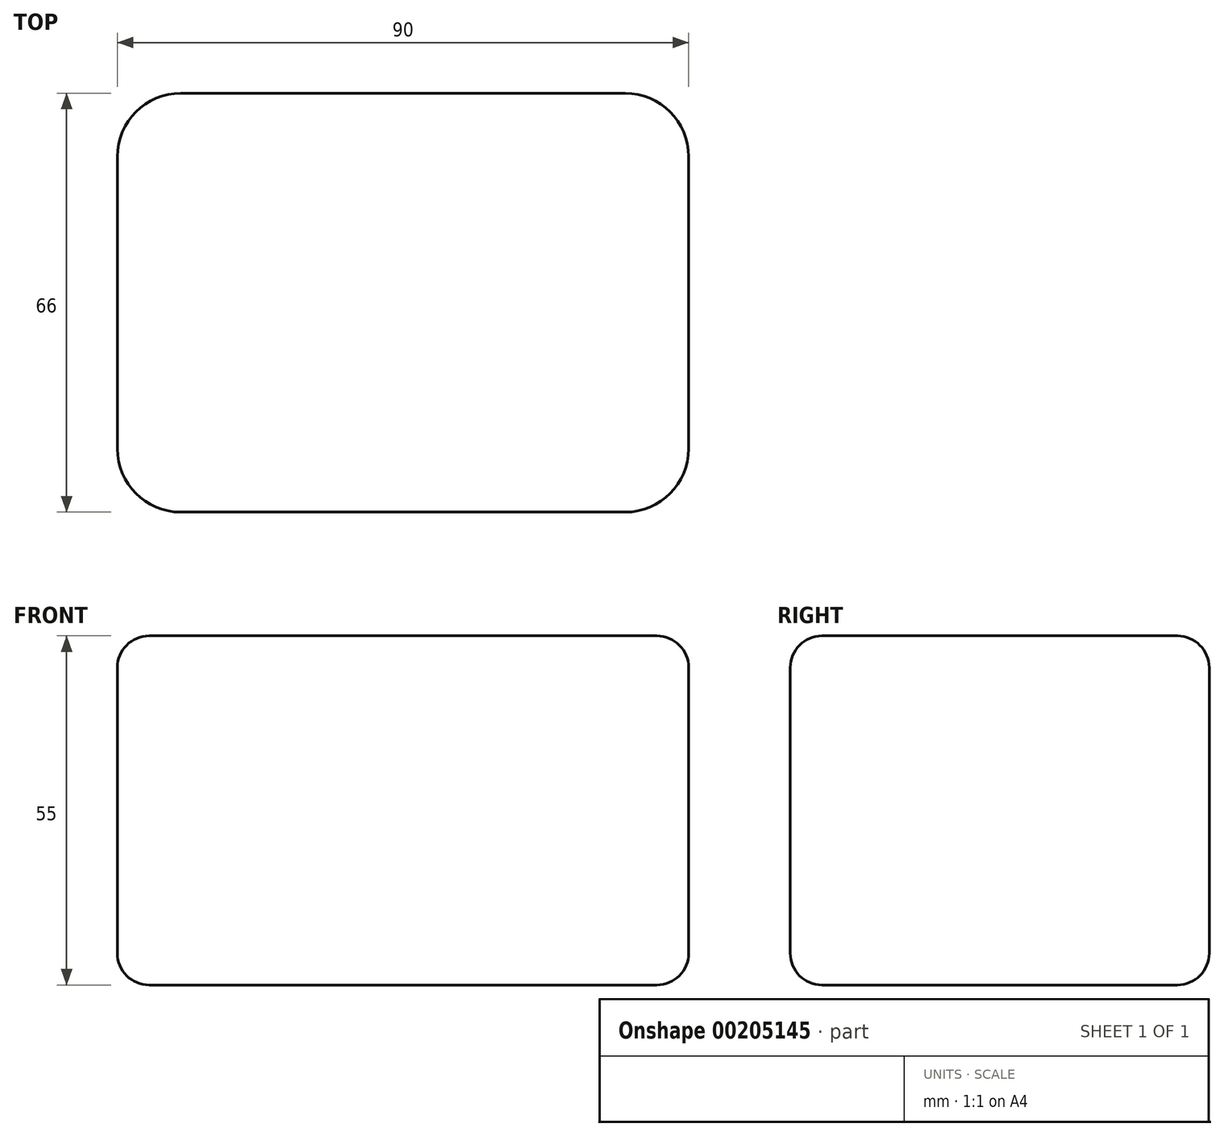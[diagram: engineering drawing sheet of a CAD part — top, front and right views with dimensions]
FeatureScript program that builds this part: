
annotation { "Feature Type Name" : "Feature", "Feature Type Description" : "" }
export const myFeature = defineFeature(function(context is Context, id is Id, definition is map)
    precondition{}
    {
        {
            var Q0;
            Q0=qCreatedBy(makeId("Top.planeOp"),FACE);
            var sketch = newSketch(context, id + "F0", { "sketchPlane" : qUnion([Q0])});
            skLineSegment(sketch, "E0.bottom", {"start": v(0, 0) * mm, "end": v(90, 0) * mm});
            skLineSegment(sketch, "E0.top", {"start": v(0, 66) * mm, "end": v(90, 66) * mm});
            skLineSegment(sketch, "E0.left", {"start": v(0, 0) * mm, "end": v(0, 66) * mm});
            skLineSegment(sketch, "E0.right", {"start": v(90, 0) * mm, "end": v(90, 66) * mm});
            skSolve(sketch);
        }
        {
            var Q0;
            Q0=makeQuery(id+"F0.imprint","IMPRINT",FACE,{"disambiguationData":[TD([[makeQuery(id+"F0.imprint","IMPRINT",EDGE,{"derivedFrom":sQuery(id+"F0.wireOp",EDGE,"E0.bottom")}),1.0]])]});
            extrude(context, id + "F1", {"entities" : qUnion([Q0]), "depth" : 55 * mm});
        }
        {
            var Q0;
            Q0=makeQuery(id+"F1.opExtrude","SWEPT_EDGE",EDGE,{"disambiguationData":[OSD([sQuery(id+"F0.wireOp",EDGE,"E0.bottom"),sQuery(id+"F0.wireOp",EDGE,"E0.right")])]});
            var Q1;
            Q1=makeQuery(id+"F1.opExtrude","SWEPT_EDGE",EDGE,{"disambiguationData":[OSD([sQuery(id+"F0.wireOp",EDGE,"E0.top"),sQuery(id+"F0.wireOp",EDGE,"E0.right")])]});
            var Q2;
            Q2=makeQuery(id+"F1.opExtrude","SWEPT_EDGE",EDGE,{"disambiguationData":[OSD([sQuery(id+"F0.wireOp",EDGE,"E0.top"),sQuery(id+"F0.wireOp",EDGE,"E0.left")])]});
            var Q3;
            Q3=makeQuery(id+"F1.opExtrude","SWEPT_EDGE",EDGE,{"disambiguationData":[OSD([sQuery(id+"F0.wireOp",EDGE,"E0.bottom"),sQuery(id+"F0.wireOp",EDGE,"E0.left")])]});
            fillet(context, id + "F2", {"entities" : qUnion([Q0, Q1, Q2, Q3]), "radius" : 10 * mm, "tangentPropagation" : true, "allowEdgeOverflow" : false});
        }
        {
            var Q0;
            Q0=makeQuery(id+"F1.opExtrude","CAP_FACE",FACE,{"disambiguationData":[OSD([sQuery(id+"F0.wireOp",EDGE,"E0.bottom"),sQuery(id+"F0.wireOp",EDGE,"E0.top"),sQuery(id+"F0.wireOp",EDGE,"E0.left"),sQuery(id+"F0.wireOp",EDGE,"E0.right")])],"isStart":true});
            var Q1;
            Q1=makeQuery(id+"F1.opExtrude","CAP_FACE",FACE,{"disambiguationData":[OSD([sQuery(id+"F0.wireOp",EDGE,"E0.bottom"),sQuery(id+"F0.wireOp",EDGE,"E0.top"),sQuery(id+"F0.wireOp",EDGE,"E0.left"),sQuery(id+"F0.wireOp",EDGE,"E0.right")])],"isStart":false});
            fillet(context, id + "F3", {"entities" : qUnion([Q0, Q1]), "radius" : 5 * mm, "tangentPropagation" : true, "allowEdgeOverflow" : false});
        }
    });
